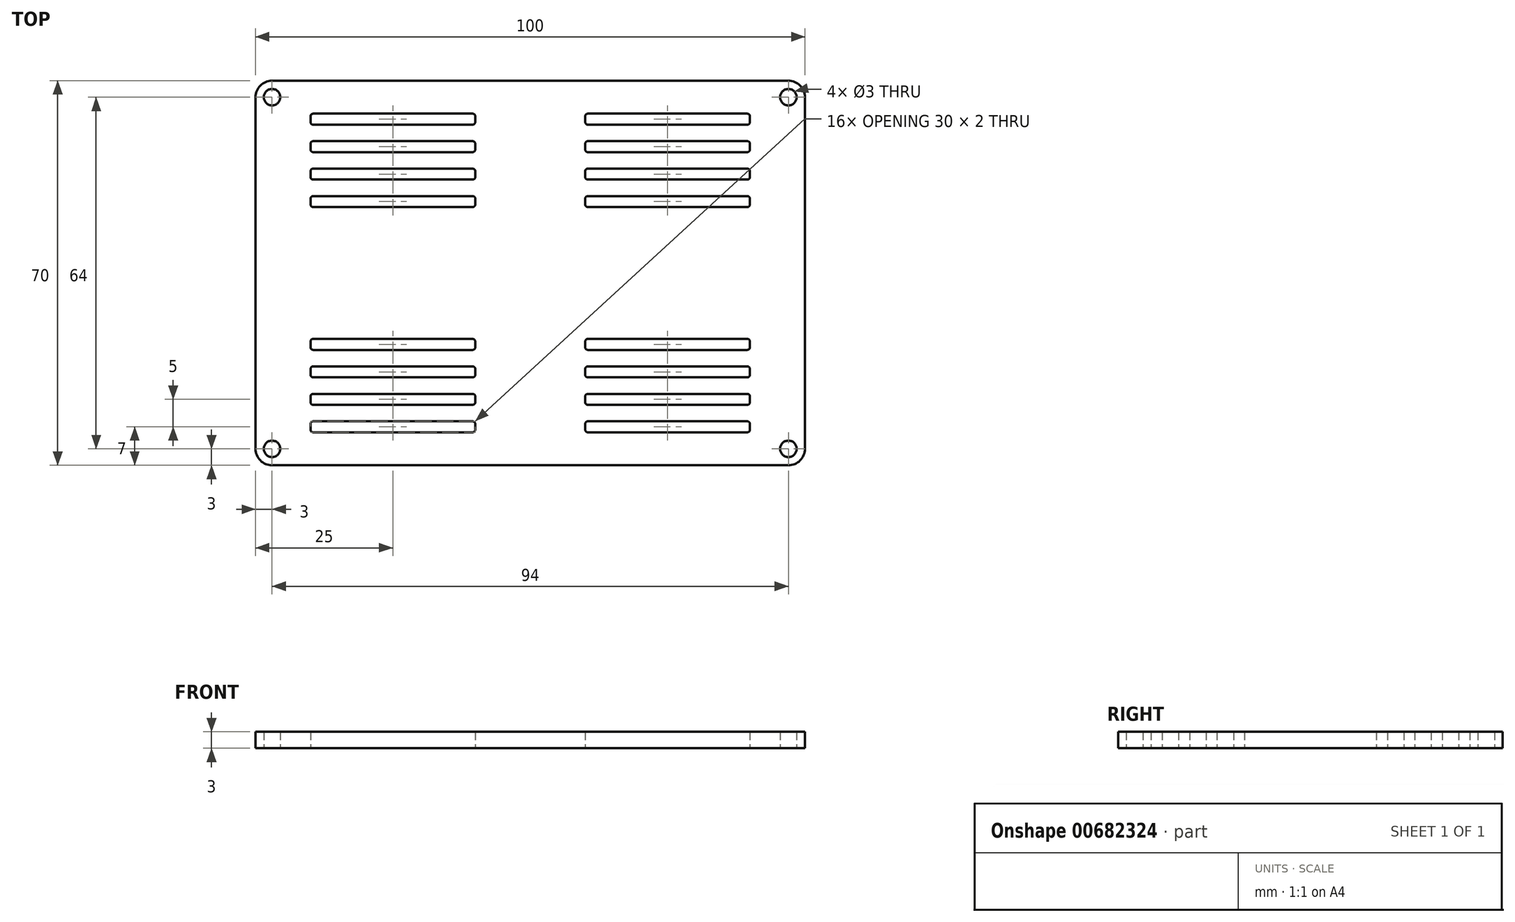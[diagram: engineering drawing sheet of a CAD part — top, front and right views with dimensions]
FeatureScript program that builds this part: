
annotation { "Feature Type Name" : "Feature", "Feature Type Description" : "" }
export const myFeature = defineFeature(function(context is Context, id is Id, definition is map)
    precondition{}
    {
        {
            var Q0;
            Q0=qCreatedBy(makeId("Top.planeOp"),FACE);
            var sketch = newSketch(context, id + "F0", { "sketchPlane" : qUnion([Q0])});
            skLineSegment(sketch, "E0.bottom", {"start": v(3, 0) * mm, "end": v(97, 0) * mm});
            skLineSegment(sketch, "E0.top", {"start": v(3, 70) * mm, "end": v(97, 70) * mm});
            skLineSegment(sketch, "E0.left", {"start": v(0, 3) * mm, "end": v(0, 67) * mm});
            skLineSegment(sketch, "E0.right", {"start": v(100, 3) * mm, "end": v(100, 67) * mm});
            skPoint(sketch, "E1.visualSharp", {"position": v(0, 70) * mm});
            skArc(sketch, "E1.filletArc", {"start": v(3, 70) * mm, "mid": v(0.88, 69.12) * mm, "end": v(0, 67) * mm});
            skPoint(sketch, "E2.visualSharp", {"position": v(100, 70) * mm});
            skArc(sketch, "E2.filletArc", {"start": v(100, 67) * mm, "mid": v(99.12, 69.12) * mm, "end": v(97, 70) * mm});
            skPoint(sketch, "E3.visualSharp", {"position": v(100, 0) * mm});
            skArc(sketch, "E3.filletArc", {"start": v(97, 0) * mm, "mid": v(99.12, 0.88) * mm, "end": v(100, 3) * mm});
            skPoint(sketch, "E4.visualSharp", {"position": v(0, 0) * mm});
            skArc(sketch, "E4.filletArc", {"start": v(0, 3) * mm, "mid": v(0.88, 0.88) * mm, "end": v(3, 0) * mm});
            skSolve(sketch);
        }
        {
            var Q0;
            Q0 = qSketchRegion(id + "F0", true);
            extrude(context, id + "F1", {"entities" : qUnion([Q0]), "depth" : 3 * mm, "offsetDistance" : 25 * mm});
        }
        {
            var Q0;
            Q0=makeQuery(id+"F1.opExtrude","CAP_FACE",FACE,{"disambiguationData":[OSD([sQuery(id+"F0.wireOp",EDGE,"E0.bottom"),sQuery(id+"F0.wireOp",EDGE,"E0.top"),sQuery(id+"F0.wireOp",EDGE,"E0.left"),sQuery(id+"F0.wireOp",EDGE,"E0.right"),sQuery(id+"F0.wireOp",EDGE,"E1.filletArc"),sQuery(id+"F0.wireOp",EDGE,"E2.filletArc"),sQuery(id+"F0.wireOp",EDGE,"E3.filletArc"),sQuery(id+"F0.wireOp",EDGE,"E4.filletArc")])],"isStart":true});
            var sketch = newSketch(context, id + "F2", { "sketchPlane" : qUnion([Q0])});
            skCircle(sketch, "E5", {"center": v(3, -67) * mm, "radius": 1.5 * mm});
            skCircle(sketch, "E6", {"center": v(3, -3) * mm, "radius": 1.5 * mm});
            skCircle(sketch, "E7", {"center": v(97, -3) * mm, "radius": 1.5 * mm});
            skCircle(sketch, "E8", {"center": v(97, -67) * mm, "radius": 1.5 * mm});
            skSolve(sketch);
        }
        {
            var Q0;
            Q0 = qSketchRegion(id + "F2", true);
            extrude(context, id + "F3", {"entities" : qUnion([Q0]), "operationType" : NewBodyOperationType.REMOVE, "oppositeDirection" : true, "depth" : 25 * mm, "offsetDistance" : 25 * mm});
        }
        {
            var Q0;
            Q0=makeQuery(id+"F1.opExtrude","CAP_FACE",FACE,{"disambiguationData":[OSD([sQuery(id+"F0.wireOp",EDGE,"E0.bottom"),sQuery(id+"F0.wireOp",EDGE,"E0.top"),sQuery(id+"F0.wireOp",EDGE,"E0.left"),sQuery(id+"F0.wireOp",EDGE,"E0.right"),sQuery(id+"F0.wireOp",EDGE,"E1.filletArc"),sQuery(id+"F0.wireOp",EDGE,"E2.filletArc"),sQuery(id+"F0.wireOp",EDGE,"E3.filletArc"),sQuery(id+"F0.wireOp",EDGE,"E4.filletArc")])],"isStart":true});
            var sketch = newSketch(context, id + "F4", { "sketchPlane" : qUnion([Q0])});
            skLineSegment(sketch, "E9", {"start": v(0, -35) * mm, "end": v(100, -35) * mm, "construction": true});
            skLineSegment(sketch, "E10", {"start": v(50, -70) * mm, "end": v(50, 0) * mm, "construction": true});
            skLineSegment(sketch, "E11.bottom", {"start": v(10.5, -64) * mm, "end": v(39.5, -64) * mm});
            skLineSegment(sketch, "E11.top", {"start": v(10.5, -62) * mm, "end": v(39.5, -62) * mm});
            skLineSegment(sketch, "E11.left", {"start": v(10, -63.5) * mm, "end": v(10, -62.5) * mm});
            skLineSegment(sketch, "E11.right", {"start": v(40, -63.5) * mm, "end": v(40, -62.5) * mm});
            skPoint(sketch, "E12.visualSharp", {"position": v(10, -64) * mm});
            skArc(sketch, "E12.filletArc", {"start": v(10, -63.5) * mm, "mid": v(10.15, -63.85) * mm, "end": v(10.5, -64) * mm});
            skPoint(sketch, "E13.visualSharp", {"position": v(10, -62) * mm});
            skArc(sketch, "E13.filletArc", {"start": v(10.5, -62) * mm, "mid": v(10.15, -62.15) * mm, "end": v(10, -62.5) * mm});
            skPoint(sketch, "E14.visualSharp", {"position": v(40, -62) * mm});
            skArc(sketch, "E14.filletArc", {"start": v(40, -62.5) * mm, "mid": v(39.85, -62.15) * mm, "end": v(39.5, -62) * mm});
            skPoint(sketch, "E15.visualSharp", {"position": v(40, -64) * mm});
            skArc(sketch, "E15.filletArc", {"start": v(39.5, -64) * mm, "mid": v(39.85, -63.85) * mm, "end": v(40, -63.5) * mm});
            skPoint(sketch, "E16.0.1.0", {"position": v(40, -57) * mm});
            skPoint(sketch, "E16.0.1.1", {"position": v(10, -59) * mm});
            skPoint(sketch, "E16.0.1.2", {"position": v(10, -57) * mm});
            skPoint(sketch, "E16.0.1.3", {"position": v(40, -59) * mm});
            skLineSegment(sketch, "E16.0.1.4", {"start": v(10.5, -57) * mm, "end": v(39.5, -57) * mm});
            skLineSegment(sketch, "E16.0.1.5", {"start": v(10.5, -59) * mm, "end": v(39.5, -59) * mm});
            skArc(sketch, "E16.0.1.6", {"start": v(10.5, -57) * mm, "mid": v(10.15, -57.15) * mm, "end": v(10, -57.5) * mm});
            skLineSegment(sketch, "E16.0.1.7", {"start": v(40, -58.5) * mm, "end": v(40, -57.5) * mm});
            skArc(sketch, "E16.0.1.8", {"start": v(39.5, -59) * mm, "mid": v(39.85, -58.85) * mm, "end": v(40, -58.5) * mm});
            skArc(sketch, "E16.0.1.9", {"start": v(40, -57.5) * mm, "mid": v(39.85, -57.15) * mm, "end": v(39.5, -57) * mm});
            skArc(sketch, "E16.0.1.10", {"start": v(10, -58.5) * mm, "mid": v(10.15, -58.85) * mm, "end": v(10.5, -59) * mm});
            skLineSegment(sketch, "E16.0.1.11", {"start": v(10, -58.5) * mm, "end": v(10, -57.5) * mm});
            skPoint(sketch, "E16.0.2.0", {"position": v(40, -52) * mm});
            skPoint(sketch, "E16.0.2.1", {"position": v(10, -54) * mm});
            skPoint(sketch, "E16.0.2.2", {"position": v(10, -52) * mm});
            skPoint(sketch, "E16.0.2.3", {"position": v(40, -54) * mm});
            skLineSegment(sketch, "E16.0.2.4", {"start": v(10.5, -52) * mm, "end": v(39.5, -52) * mm});
            skLineSegment(sketch, "E16.0.2.5", {"start": v(10.5, -54) * mm, "end": v(39.5, -54) * mm});
            skArc(sketch, "E16.0.2.6", {"start": v(10.5, -52) * mm, "mid": v(10.15, -52.15) * mm, "end": v(10, -52.5) * mm});
            skLineSegment(sketch, "E16.0.2.7", {"start": v(40, -53.5) * mm, "end": v(40, -52.5) * mm});
            skArc(sketch, "E16.0.2.8", {"start": v(39.5, -54) * mm, "mid": v(39.85, -53.85) * mm, "end": v(40, -53.5) * mm});
            skArc(sketch, "E16.0.2.9", {"start": v(40, -52.5) * mm, "mid": v(39.85, -52.15) * mm, "end": v(39.5, -52) * mm});
            skArc(sketch, "E16.0.2.10", {"start": v(10, -53.5) * mm, "mid": v(10.15, -53.85) * mm, "end": v(10.5, -54) * mm});
            skLineSegment(sketch, "E16.0.2.11", {"start": v(10, -53.5) * mm, "end": v(10, -52.5) * mm});
            skPoint(sketch, "E16.0.3.0", {"position": v(40, -47) * mm});
            skPoint(sketch, "E16.0.3.1", {"position": v(10, -49) * mm});
            skPoint(sketch, "E16.0.3.2", {"position": v(10, -47) * mm});
            skPoint(sketch, "E16.0.3.3", {"position": v(40, -49) * mm});
            skLineSegment(sketch, "E16.0.3.4", {"start": v(10.5, -47) * mm, "end": v(39.5, -47) * mm});
            skLineSegment(sketch, "E16.0.3.5", {"start": v(10.5, -49) * mm, "end": v(39.5, -49) * mm});
            skArc(sketch, "E16.0.3.6", {"start": v(10.5, -47) * mm, "mid": v(10.15, -47.15) * mm, "end": v(10, -47.5) * mm});
            skLineSegment(sketch, "E16.0.3.7", {"start": v(40, -48.5) * mm, "end": v(40, -47.5) * mm});
            skArc(sketch, "E16.0.3.8", {"start": v(39.5, -49) * mm, "mid": v(39.85, -48.85) * mm, "end": v(40, -48.5) * mm});
            skArc(sketch, "E16.0.3.9", {"start": v(40, -47.5) * mm, "mid": v(39.85, -47.15) * mm, "end": v(39.5, -47) * mm});
            skArc(sketch, "E16.0.3.10", {"start": v(10, -48.5) * mm, "mid": v(10.15, -48.85) * mm, "end": v(10.5, -49) * mm});
            skLineSegment(sketch, "E16.0.3.11", {"start": v(10, -48.5) * mm, "end": v(10, -47.5) * mm});
            skLineSegment(sketch, "E16.direction1", {"start": v(10, -64) * mm, "end": v(35, -64) * mm, "construction": true});
            skLineSegment(sketch, "E16.direction2", {"start": v(10, -64) * mm, "end": v(10, -59) * mm, "construction": true});
            skArc(sketch, "E17.MirrorCS", {"start": v(10, -6.5) * mm, "mid": v(10.15, -6.15) * mm, "end": v(10.5, -6) * mm});
            skLineSegment(sketch, "E18.MirrorCS", {"start": v(10, -21.5) * mm, "end": v(10, -22.5) * mm});
            skLineSegment(sketch, "E19.MirrorCS", {"start": v(10, -6.5) * mm, "end": v(10, -7.5) * mm});
            skLineSegment(sketch, "E20.MirrorCS", {"start": v(40, -16.5) * mm, "end": v(40, -17.5) * mm});
            skArc(sketch, "E21.MirrorCS", {"start": v(40, -17.5) * mm, "mid": v(39.85, -17.85) * mm, "end": v(39.5, -18) * mm});
            skArc(sketch, "E22.MirrorCS", {"start": v(10, -16.5) * mm, "mid": v(10.15, -16.15) * mm, "end": v(10.5, -16) * mm});
            skLineSegment(sketch, "E23.MirrorCS", {"start": v(10, -16.5) * mm, "end": v(10, -17.5) * mm});
            skArc(sketch, "E24.MirrorCS", {"start": v(10.5, -23) * mm, "mid": v(10.15, -22.85) * mm, "end": v(10, -22.5) * mm});
            skLineSegment(sketch, "E25.MirrorCS", {"start": v(10, -11.5) * mm, "end": v(10, -12.5) * mm});
            skArc(sketch, "E26.MirrorCS", {"start": v(40, -22.5) * mm, "mid": v(39.85, -22.85) * mm, "end": v(39.5, -23) * mm});
            skLineSegment(sketch, "E27.MirrorCS", {"start": v(40, -6.5) * mm, "end": v(40, -7.5) * mm});
            skArc(sketch, "E28.MirrorCS", {"start": v(10.5, -18) * mm, "mid": v(10.15, -17.85) * mm, "end": v(10, -17.5) * mm});
            skLineSegment(sketch, "E29.MirrorCS", {"start": v(40, -21.5) * mm, "end": v(40, -22.5) * mm});
            skArc(sketch, "E30.MirrorCS", {"start": v(39.5, -21) * mm, "mid": v(39.85, -21.15) * mm, "end": v(40, -21.5) * mm});
            skArc(sketch, "E31.MirrorCS", {"start": v(39.5, -11) * mm, "mid": v(39.85, -11.15) * mm, "end": v(40, -11.5) * mm});
            skLineSegment(sketch, "E32.MirrorCS", {"start": v(40, -11.5) * mm, "end": v(40, -12.5) * mm});
            skArc(sketch, "E33.MirrorCS", {"start": v(40, -12.5) * mm, "mid": v(39.85, -12.85) * mm, "end": v(39.5, -13) * mm});
            skArc(sketch, "E34.MirrorCS", {"start": v(10, -11.5) * mm, "mid": v(10.15, -11.15) * mm, "end": v(10.5, -11) * mm});
            skArc(sketch, "E35.MirrorCS", {"start": v(39.5, -16) * mm, "mid": v(39.85, -16.15) * mm, "end": v(40, -16.5) * mm});
            skArc(sketch, "E36.MirrorCS", {"start": v(40, -7.5) * mm, "mid": v(39.85, -7.85) * mm, "end": v(39.5, -8) * mm});
            skArc(sketch, "E37.MirrorCS", {"start": v(10, -21.5) * mm, "mid": v(10.15, -21.15) * mm, "end": v(10.5, -21) * mm});
            skArc(sketch, "E38.MirrorCS", {"start": v(10.5, -13) * mm, "mid": v(10.15, -12.85) * mm, "end": v(10, -12.5) * mm});
            skArc(sketch, "E39.MirrorCS", {"start": v(10.5, -8) * mm, "mid": v(10.15, -7.85) * mm, "end": v(10, -7.5) * mm});
            skArc(sketch, "E40.MirrorCS", {"start": v(39.5, -6) * mm, "mid": v(39.85, -6.15) * mm, "end": v(40, -6.5) * mm});
            skLineSegment(sketch, "E41.MirrorCS", {"start": v(10, -6) * mm, "end": v(10, -11) * mm, "construction": true});
            skLineSegment(sketch, "E42.MirrorCS", {"start": v(10.5, -18) * mm, "end": v(39.5, -18) * mm});
            skLineSegment(sketch, "E43.MirrorCS", {"start": v(10, -6) * mm, "end": v(35, -6) * mm, "construction": true});
            skLineSegment(sketch, "E44.MirrorCS", {"start": v(10.5, -16) * mm, "end": v(39.5, -16) * mm});
            skPoint(sketch, "E45.MirrorP", {"position": v(40, -11) * mm});
            skPoint(sketch, "E46.MirrorP", {"position": v(40, -21) * mm});
            skPoint(sketch, "E47.MirrorP", {"position": v(10, -6) * mm});
            skPoint(sketch, "E48.MirrorP", {"position": v(10, -11) * mm});
            skPoint(sketch, "E49.MirrorP", {"position": v(40, -18) * mm});
            skPoint(sketch, "E50.MirrorP", {"position": v(10, -21) * mm});
            skPoint(sketch, "E51.MirrorP", {"position": v(10, -13) * mm});
            skPoint(sketch, "E52.MirrorP", {"position": v(10, -16) * mm});
            skPoint(sketch, "E53.MirrorP", {"position": v(10, -23) * mm});
            skLineSegment(sketch, "E54.MirrorCS", {"start": v(10.5, -8) * mm, "end": v(39.5, -8) * mm});
            skLineSegment(sketch, "E55.MirrorCS", {"start": v(10.5, -6) * mm, "end": v(39.5, -6) * mm});
            skPoint(sketch, "E56.MirrorP", {"position": v(40, -8) * mm});
            skLineSegment(sketch, "E57.MirrorCS", {"start": v(10.5, -23) * mm, "end": v(39.5, -23) * mm});
            skPoint(sketch, "E58.MirrorP", {"position": v(40, -6) * mm});
            skPoint(sketch, "E59.MirrorP", {"position": v(40, -23) * mm});
            skLineSegment(sketch, "E60.MirrorCS", {"start": v(10.5, -21) * mm, "end": v(39.5, -21) * mm});
            skPoint(sketch, "E61.MirrorP", {"position": v(10, -18) * mm});
            skPoint(sketch, "E62.MirrorP", {"position": v(10, -8) * mm});
            skPoint(sketch, "E63.MirrorP", {"position": v(40, -13) * mm});
            skPoint(sketch, "E64.MirrorP", {"position": v(40, -16) * mm});
            skLineSegment(sketch, "E65.MirrorCS", {"start": v(10.5, -13) * mm, "end": v(39.5, -13) * mm});
            skLineSegment(sketch, "E66.MirrorCS", {"start": v(10.5, -11) * mm, "end": v(39.5, -11) * mm});
            skArc(sketch, "E67.MirrorCS", {"start": v(89.5, -18) * mm, "mid": v(89.85, -17.85) * mm, "end": v(90, -17.5) * mm});
            skLineSegment(sketch, "E68.MirrorCS", {"start": v(90, -16.5) * mm, "end": v(90, -17.5) * mm});
            skArc(sketch, "E69.MirrorCS", {"start": v(60, -62.5) * mm, "mid": v(60.15, -62.15) * mm, "end": v(60.5, -62) * mm});
            skArc(sketch, "E70.MirrorCS", {"start": v(89.5, -62) * mm, "mid": v(89.85, -62.15) * mm, "end": v(90, -62.5) * mm});
            skLineSegment(sketch, "E71.MirrorCS", {"start": v(60, -63.5) * mm, "end": v(60, -62.5) * mm});
            skLineSegment(sketch, "E72.MirrorCS", {"start": v(90, -6.5) * mm, "end": v(90, -7.5) * mm});
            skLineSegment(sketch, "E73.MirrorCS", {"start": v(90, -63.5) * mm, "end": v(90, -62.5) * mm});
            skArc(sketch, "E74.MirrorCS", {"start": v(90, -6.5) * mm, "mid": v(89.85, -6.15) * mm, "end": v(89.5, -6) * mm});
            skArc(sketch, "E75.MirrorCS", {"start": v(90, -63.5) * mm, "mid": v(89.85, -63.85) * mm, "end": v(89.5, -64) * mm});
            skLineSegment(sketch, "E76.MirrorCS", {"start": v(90, -58.5) * mm, "end": v(90, -57.5) * mm});
            skLineSegment(sketch, "E77.MirrorCS", {"start": v(90, -48.5) * mm, "end": v(90, -47.5) * mm});
            skArc(sketch, "E78.MirrorCS", {"start": v(60.5, -21) * mm, "mid": v(60.15, -21.15) * mm, "end": v(60, -21.5) * mm});
            skArc(sketch, "E79.MirrorCS", {"start": v(60, -47.5) * mm, "mid": v(60.15, -47.15) * mm, "end": v(60.5, -47) * mm});
            skLineSegment(sketch, "E80.MirrorCS", {"start": v(60, -11.5) * mm, "end": v(60, -12.5) * mm});
            skLineSegment(sketch, "E81.MirrorCS", {"start": v(60, -53.5) * mm, "end": v(60, -52.5) * mm});
            skLineSegment(sketch, "E82.MirrorCS", {"start": v(90, -21.5) * mm, "end": v(90, -22.5) * mm});
            skArc(sketch, "E83.MirrorCS", {"start": v(60.5, -49) * mm, "mid": v(60.15, -48.85) * mm, "end": v(60, -48.5) * mm});
            skArc(sketch, "E84.MirrorCS", {"start": v(90, -11.5) * mm, "mid": v(89.85, -11.15) * mm, "end": v(89.5, -11) * mm});
            skLineSegment(sketch, "E85.MirrorCS", {"start": v(60, -6.5) * mm, "end": v(60, -7.5) * mm});
            skArc(sketch, "E86.MirrorCS", {"start": v(90, -21.5) * mm, "mid": v(89.85, -21.15) * mm, "end": v(89.5, -21) * mm});
            skArc(sketch, "E87.MirrorCS", {"start": v(90, -53.5) * mm, "mid": v(89.85, -53.85) * mm, "end": v(89.5, -54) * mm});
            skArc(sketch, "E88.MirrorCS", {"start": v(60, -17.5) * mm, "mid": v(60.15, -17.85) * mm, "end": v(60.5, -18) * mm});
            skArc(sketch, "E89.MirrorCS", {"start": v(89.5, -8) * mm, "mid": v(89.85, -7.85) * mm, "end": v(90, -7.5) * mm});
            skArc(sketch, "E90.MirrorCS", {"start": v(89.5, -47) * mm, "mid": v(89.85, -47.15) * mm, "end": v(90, -47.5) * mm});
            skLineSegment(sketch, "E91.MirrorCS", {"start": v(90, -11.5) * mm, "end": v(90, -12.5) * mm});
            skArc(sketch, "E92.MirrorCS", {"start": v(60, -7.5) * mm, "mid": v(60.15, -7.85) * mm, "end": v(60.5, -8) * mm});
            skArc(sketch, "E93.MirrorCS", {"start": v(89.5, -57) * mm, "mid": v(89.85, -57.15) * mm, "end": v(90, -57.5) * mm});
            skArc(sketch, "E94.MirrorCS", {"start": v(60.5, -64) * mm, "mid": v(60.15, -63.85) * mm, "end": v(60, -63.5) * mm});
            skLineSegment(sketch, "E95.MirrorCS", {"start": v(60, -48.5) * mm, "end": v(60, -47.5) * mm});
            skArc(sketch, "E96.MirrorCS", {"start": v(60.5, -11) * mm, "mid": v(60.15, -11.15) * mm, "end": v(60, -11.5) * mm});
            skLineSegment(sketch, "E97.MirrorCS", {"start": v(60, -16.5) * mm, "end": v(60, -17.5) * mm});
            skArc(sketch, "E98.MirrorCS", {"start": v(60, -22.5) * mm, "mid": v(60.15, -22.85) * mm, "end": v(60.5, -23) * mm});
            skArc(sketch, "E99.MirrorCS", {"start": v(60, -12.5) * mm, "mid": v(60.15, -12.85) * mm, "end": v(60.5, -13) * mm});
            skArc(sketch, "E100.MirrorCS", {"start": v(90, -58.5) * mm, "mid": v(89.85, -58.85) * mm, "end": v(89.5, -59) * mm});
            skArc(sketch, "E101.MirrorCS", {"start": v(60.5, -6) * mm, "mid": v(60.15, -6.15) * mm, "end": v(60, -6.5) * mm});
            skLineSegment(sketch, "E102.MirrorCS", {"start": v(60, -21.5) * mm, "end": v(60, -22.5) * mm});
            skArc(sketch, "E103.MirrorCS", {"start": v(89.5, -52) * mm, "mid": v(89.85, -52.15) * mm, "end": v(90, -52.5) * mm});
            skLineSegment(sketch, "E104.MirrorCS", {"start": v(60, -58.5) * mm, "end": v(60, -57.5) * mm});
            skArc(sketch, "E105.MirrorCS", {"start": v(90, -16.5) * mm, "mid": v(89.85, -16.15) * mm, "end": v(89.5, -16) * mm});
            skArc(sketch, "E106.MirrorCS", {"start": v(60.5, -59) * mm, "mid": v(60.15, -58.85) * mm, "end": v(60, -58.5) * mm});
            skLineSegment(sketch, "E107.MirrorCS", {"start": v(90, -53.5) * mm, "end": v(90, -52.5) * mm});
            skArc(sketch, "E108.MirrorCS", {"start": v(60, -52.5) * mm, "mid": v(60.15, -52.15) * mm, "end": v(60.5, -52) * mm});
            skArc(sketch, "E109.MirrorCS", {"start": v(89.5, -13) * mm, "mid": v(89.85, -12.85) * mm, "end": v(90, -12.5) * mm});
            skArc(sketch, "E110.MirrorCS", {"start": v(60.5, -54) * mm, "mid": v(60.15, -53.85) * mm, "end": v(60, -53.5) * mm});
            skArc(sketch, "E111.MirrorCS", {"start": v(89.5, -23) * mm, "mid": v(89.85, -22.85) * mm, "end": v(90, -22.5) * mm});
            skArc(sketch, "E112.MirrorCS", {"start": v(60.5, -16) * mm, "mid": v(60.15, -16.15) * mm, "end": v(60, -16.5) * mm});
            skArc(sketch, "E113.MirrorCS", {"start": v(60, -57.5) * mm, "mid": v(60.15, -57.15) * mm, "end": v(60.5, -57) * mm});
            skArc(sketch, "E114.MirrorCS", {"start": v(90, -48.5) * mm, "mid": v(89.85, -48.85) * mm, "end": v(89.5, -49) * mm});
            skLineSegment(sketch, "E115.MirrorCS", {"start": v(90, -64) * mm, "end": v(90, -59) * mm, "construction": true});
            skLineSegment(sketch, "E116.MirrorCS", {"start": v(90, -6) * mm, "end": v(90, -11) * mm, "construction": true});
            skLineSegment(sketch, "E117.MirrorCS", {"start": v(89.5, -6) * mm, "end": v(60.5, -6) * mm});
            skPoint(sketch, "E118.MirrorP", {"position": v(90, -59) * mm});
            skPoint(sketch, "E119.MirrorP", {"position": v(90, -49) * mm});
            skPoint(sketch, "E120.MirrorP", {"position": v(60, -8) * mm});
            skPoint(sketch, "E121.MirrorP", {"position": v(90, -8) * mm});
            skLineSegment(sketch, "E122.MirrorCS", {"start": v(89.5, -54) * mm, "end": v(60.5, -54) * mm});
            skLineSegment(sketch, "E123.MirrorCS", {"start": v(89.5, -16) * mm, "end": v(60.5, -16) * mm});
            skLineSegment(sketch, "E124.MirrorCS", {"start": v(89.5, -21) * mm, "end": v(60.5, -21) * mm});
            skPoint(sketch, "E125.MirrorP", {"position": v(60, -57) * mm});
            skPoint(sketch, "E126.MirrorP", {"position": v(60, -47) * mm});
            skPoint(sketch, "E127.MirrorP", {"position": v(90, -23) * mm});
            skPoint(sketch, "E128.MirrorP", {"position": v(60, -16) * mm});
            skLineSegment(sketch, "E129.MirrorCS", {"start": v(90, -6) * mm, "end": v(65, -6) * mm, "construction": true});
            skLineSegment(sketch, "E130.MirrorCS", {"start": v(89.5, -11) * mm, "end": v(60.5, -11) * mm});
            skPoint(sketch, "E131.MirrorP", {"position": v(90, -62) * mm});
            skPoint(sketch, "E132.MirrorP", {"position": v(90, -52) * mm});
            skPoint(sketch, "E133.MirrorP", {"position": v(60, -18) * mm});
            skPoint(sketch, "E134.MirrorP", {"position": v(60, -62) * mm});
            skPoint(sketch, "E135.MirrorP", {"position": v(90, -13) * mm});
            skLineSegment(sketch, "E136.MirrorCS", {"start": v(89.5, -47) * mm, "end": v(60.5, -47) * mm});
            skPoint(sketch, "E137.MirrorP", {"position": v(60, -64) * mm});
            skPoint(sketch, "E138.MirrorP", {"position": v(60, -59) * mm});
            skPoint(sketch, "E139.MirrorP", {"position": v(60, -49) * mm});
            skPoint(sketch, "E140.MirrorP", {"position": v(60, -23) * mm});
            skPoint(sketch, "E141.MirrorP", {"position": v(60, -21) * mm});
            skPoint(sketch, "E142.MirrorP", {"position": v(90, -54) * mm});
            skLineSegment(sketch, "E143.MirrorCS", {"start": v(89.5, -59) * mm, "end": v(60.5, -59) * mm});
            skLineSegment(sketch, "E144.MirrorCS", {"start": v(89.5, -57) * mm, "end": v(60.5, -57) * mm});
            skLineSegment(sketch, "E145.MirrorCS", {"start": v(89.5, -23) * mm, "end": v(60.5, -23) * mm});
            skLineSegment(sketch, "E146.MirrorCS", {"start": v(89.5, -62) * mm, "end": v(60.5, -62) * mm});
            skLineSegment(sketch, "E147.MirrorCS", {"start": v(89.5, -18) * mm, "end": v(60.5, -18) * mm});
            skPoint(sketch, "E148.MirrorP", {"position": v(60, -52) * mm});
            skPoint(sketch, "E149.MirrorP", {"position": v(90, -6) * mm});
            skPoint(sketch, "E150.MirrorP", {"position": v(90, -47) * mm});
            skPoint(sketch, "E151.MirrorP", {"position": v(60, -13) * mm});
            skPoint(sketch, "E152.MirrorP", {"position": v(90, -18) * mm});
            skPoint(sketch, "E153.MirrorP", {"position": v(90, -11) * mm});
            skLineSegment(sketch, "E154.MirrorCS", {"start": v(90, -64) * mm, "end": v(65, -64) * mm, "construction": true});
            skLineSegment(sketch, "E155.MirrorCS", {"start": v(89.5, -52) * mm, "end": v(60.5, -52) * mm});
            skPoint(sketch, "E156.MirrorP", {"position": v(60, -11) * mm});
            skPoint(sketch, "E157.MirrorP", {"position": v(90, -21) * mm});
            skPoint(sketch, "E158.MirrorP", {"position": v(90, -16) * mm});
            skLineSegment(sketch, "E159.MirrorCS", {"start": v(89.5, -13) * mm, "end": v(60.5, -13) * mm});
            skLineSegment(sketch, "E160.MirrorCS", {"start": v(89.5, -64) * mm, "end": v(60.5, -64) * mm});
            skPoint(sketch, "E161.MirrorP", {"position": v(60, -54) * mm});
            skPoint(sketch, "E162.MirrorP", {"position": v(90, -64) * mm});
            skLineSegment(sketch, "E163.MirrorCS", {"start": v(89.5, -8) * mm, "end": v(60.5, -8) * mm});
            skPoint(sketch, "E164.MirrorP", {"position": v(60, -6) * mm});
            skLineSegment(sketch, "E165.MirrorCS", {"start": v(89.5, -49) * mm, "end": v(60.5, -49) * mm});
            skPoint(sketch, "E166.MirrorP", {"position": v(90, -57) * mm});
            skSolve(sketch);
        }
        {
            var Q0;
            Q0 = qSketchRegion(id + "F4", true);
            extrude(context, id + "F5", {"entities" : qUnion([Q0]), "operationType" : NewBodyOperationType.REMOVE, "oppositeDirection" : true, "depth" : 25 * mm, "offsetDistance" : 25 * mm});
        }
    });
